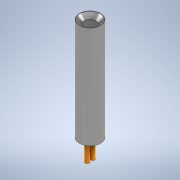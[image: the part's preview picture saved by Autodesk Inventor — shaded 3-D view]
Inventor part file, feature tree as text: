
AUTODESK INVENTOR PART (.ipt)
format: ipt  version: 2020 (Build 240168000, 168)  size: 116,224 bytes
history: native  units: mm
features: extrude x3, sketch x3, chamfer x1
ambient origin geometry x8: Origin, YZ Plane, XZ Plane, XY Plane, X Axis, Y Axis, Z Axis, Center Point
bodies: Solid1 (feature_tree)
feature tree (7):
  extrude  "Extrusion1"  Depth=76.2mm TaperAngle=0.0deg
  extrude  "Extrusion2"  Depth=3.0mm TaperAngle=0.0deg
  chamfer  "Chamfer1"  Distance=3.0mm Angle=45.0deg
  extrude  "Extrusion3"  Depth=3.0mm
  sketch  "Sketch1"  dims[d0=15.875mm d1=76.2mm d2=0.0mm]
  sketch  "Sketch2"  dims[d3=9.0mm d4=3.0mm d5=0.0mm d6=3.0mm d7=2.0mm d8=45.0deg]
  sketch  "Sketch3"  dims[d9=3.0mm d10=3.0mm d11=2.0mm d12=2.0mm d13=15.0mm d14=0.0mm]
